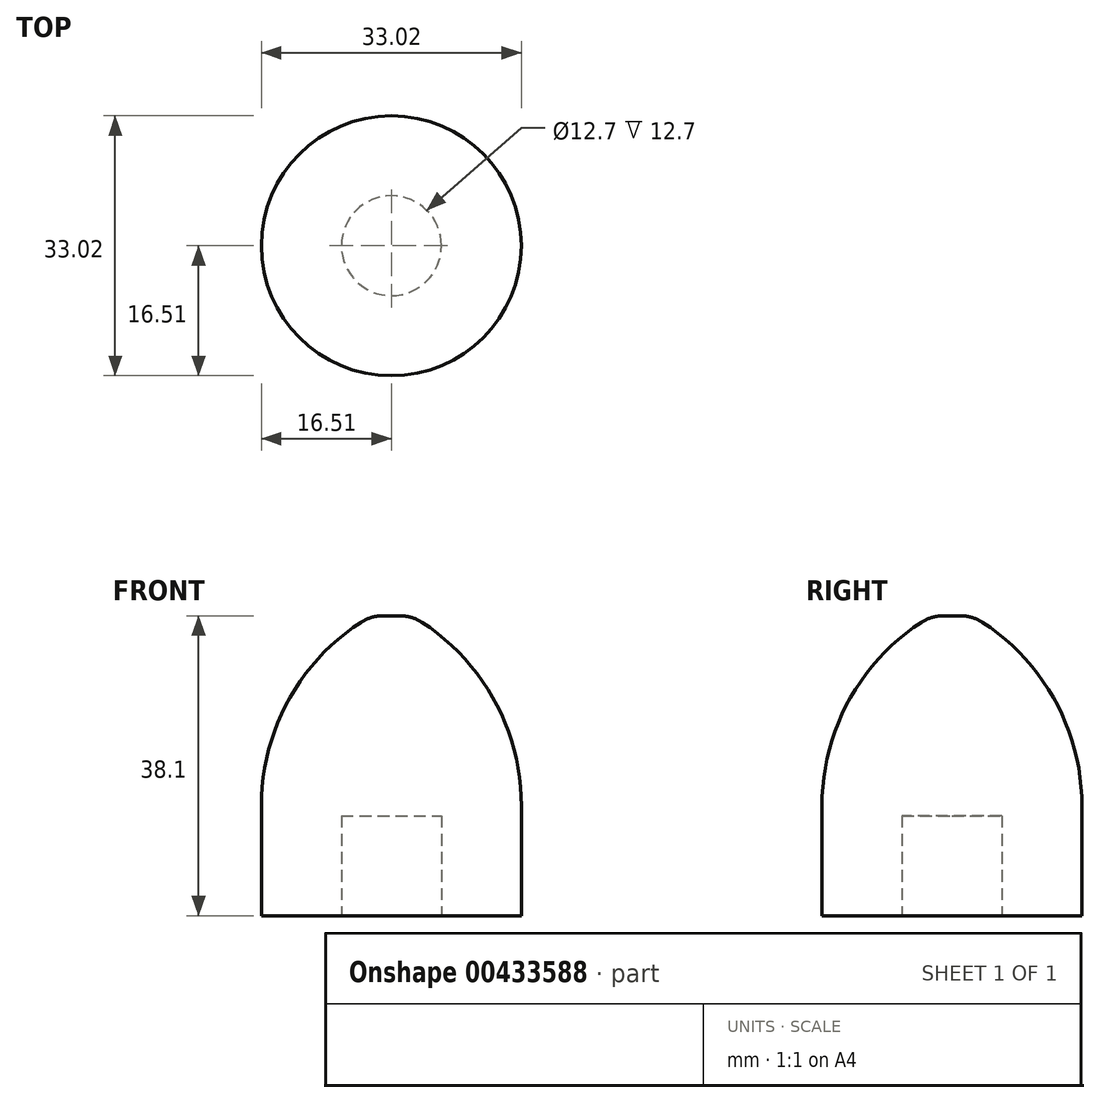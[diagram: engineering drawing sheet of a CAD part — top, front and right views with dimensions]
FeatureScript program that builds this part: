
annotation { "Feature Type Name" : "Feature", "Feature Type Description" : "" }
export const myFeature = defineFeature(function(context is Context, id is Id, definition is map)
    precondition{}
    {
        {
            var Q0;
            Q0=qCreatedBy(makeId("Front.planeOp"),FACE);
            var sketch = newSketch(context, id + "F0", { "sketchPlane" : qUnion([Q0])});
            skLineSegment(sketch, "E0", {"start": v(0, 0) * mm, "end": v(0, 38.1) * mm});
            skLineSegment(sketch, "E1", {"start": v(0, 0) * mm, "end": v(16.51, 0) * mm});
            skLineSegment(sketch, "E2", {"start": v(16.51, 0) * mm, "end": v(16.51, 13.97) * mm});
            skLineSegment(sketch, "E3", {"start": v(0, 38.1) * mm, "end": v(2.54, 38.1) * mm});
            skArc(sketch, "E4", {"start": v(16.51, 13.97) * mm, "mid": v(12.77, 27.91) * mm, "end": v(2.54, 38.1) * mm});
            skSolve(sketch);
        }
        {
            var Q0;
            Q0=makeQuery(id+"F0.imprint","IMPRINT",FACE,{"disambiguationData":[TD([[makeQuery(id+"F0.imprint","IMPRINT",EDGE,{"derivedFrom":sQuery(id+"F0.wireOp",EDGE,"E0")}),-1.0]])]});
            var Q1;
            Q1=sQuery(id+"F0.wireOp",EDGE,"E0");
            revolve(context, id + "F1", {"entities" : qUnion([Q0]), "axis" : qUnion([Q1]), "revolveType" : RevolveType.FULL});
        }
        {
            var Q0;
            Q0=makeQuery(id+"F1.opRevolve","SWEPT_EDGE",EDGE,{"disambiguationData":[OSD([sQuery(id+"F0.wireOp",EDGE,"E3"),sQuery(id+"F0.wireOp",EDGE,"E4")])]});
            fillet(context, id + "F2", {"entities" : qUnion([Q0]), "radius" : 5.08 * mm, "tangentPropagation" : true, "allowEdgeOverflow" : false});
        }
        {
            var Q0;
            Q0=makeQuery(id+"F1.opRevolve","SWEPT_FACE",FACE,{"disambiguationData":[OSD([sQuery(id+"F0.wireOp",EDGE,"E1")])]});
            var sketch = newSketch(context, id + "F3", { "sketchPlane" : qUnion([Q0])});
            skCircle(sketch, "E5", {"center": v(0, 0) * mm, "radius": 6.35 * mm});
            skSolve(sketch);
        }
        {
            var Q0;
            Q0=makeQuery(id+"F3.imprint","IMPRINT",FACE,{"disambiguationData":[TD([[makeQuery(id+"F3.imprint","IMPRINT",EDGE,{"derivedFrom":sQuery(id+"F3.wireOp",EDGE,"E5")}),1.0]])]});
            extrude(context, id + "F4", {"entities" : qUnion([Q0]), "operationType" : NewBodyOperationType.REMOVE, "oppositeDirection" : true, "depth" : 12.7 * mm});
        }
    });
